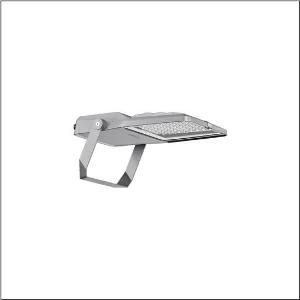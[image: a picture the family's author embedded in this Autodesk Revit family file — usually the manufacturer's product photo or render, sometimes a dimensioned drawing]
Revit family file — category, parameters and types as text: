
# Revit family: floodlight_fl_21_iq_mini___pl64_5xa7772c1e1a_659a
name_source: partatom
category: Lighting Fixtures
units: mm (PartAtom-declared; Revit-internal decimal feet)

## family parameters
Cut with Voids When Loaded = No
Host = Face
Light Source = No
Part Type = Normal
Room Calculation Point = No
Round Connector Dimension = Use Diameter
Shared = No

## types (1)
- --- (1 x LED, 9770 lm, 87.2 W, 2200K)
    Apparent Load = 87 VA
    CIE Flux Codes = 28 80 98 100 100
    Color Rendering = 70
    Color Temperature = 2200K
    Default Elevation = 1800 mm
    Description = Floodlight FL 21 iQ mini, floodlight, primary light control with lens, of PMMA, primary optical cover: protective disc, of toughened safety glass, transparent, light distribution: PL64, light emission: direct distribution, installation type: surface-mounted, LED, High Power LED, rated luminous flux: 9.770lm, luminous efficacy: 112lm/W, light colour: 722, colour temperature: 2200K, control: Street-Remote, Auto-Match, Temp-Guard, Night-Set, Smart-Wire, Desk-Remote (wireless, voltage-free reading and setting of iQ features in the workshop via application-optimized NFC function/RFID function), optimised constant luminous flux control (CLO 2.0), with terminal, 6-pole, mains connection: 220..240V, AC, 50/60Hz, start of lifetime: 87W, end of service life: 92W, reduction: 40W, luminaire housing, of diecast aluminium, powder-coated, Siteco® metallic grey (DB 702S), corrosivity category C5 mid according to DIN EN ISO 12944, sealing non-destructively replaceable, mounting bracket, of steel, galvanised, powder-coated, Siteco® metallic grey (DB 702S), protection rating (complete): IP66, insulation class (complete): insulation class II (safety insulation), certification: CE, ENEC, VDE, protection symbol: D, impact resistance: IK08, permissible operating ambient temperature: -40..+40°C, permissible operating ambient temperature for outdoor applications: -40..+50°C, standard: DIN EN 12944, LABS conformity tested according to VDMA 24364:2018-05, packaging unit: 1 piece

Light Distribution: PL64
    Height = 70 mm
    Lamp = 1 x LED
    Lamp Light Flux = 9770 lm
    Lamp Power = 87.2 W
    Lamp count = 1
    Length = 485 mm
    Luminous efficacy = 112 lm/W
    Manufacturer = Siteco
    ModVariant = No
    Model = 5XA7772C1E1A
    Number of Poles = 1
    OnlyDefault = Yes
    Power Factor = 1
    Product Name = Floodlight FL 21 iQ mini | PL64
    Product group = floodlight | pylon annexe
    ProductGroupID = 6200
    Protection Class = Protection class II
    Protection Degree = IP 66
    RLX_Detail_Level = 1
    RLX_Emergency_Light_Flux = 0 lm
    RLX_Emergency_Type = 0
    RLX_Emergency_Type_DB = No
    RlxData = <blob elided: 96261 chars, md5=eefbe549>
    Socket = socket
    Standby Power = 0 W
    System Light Flux = 9770 lm
    System Power = 87 W
    Type Comments = factory setting: luminous flux: 100 % | dim-lin: 254 | 456 mA
    Type Image = l_1006845.jpg
    URL = http://relux.com
    VarID = @adj_116621
    Voltage = 0 V
    Weight = 0.00 kg
    Width = 337 mm

## geometry (parser evidence)
native form markers: Blend x4, Sweep x14
no freeform markers — native parametric forms only
